# Revit family: Window-Exterior-Simpson-French-Sidelight
name_source: partatom
category: Windows
revit_build: Autodesk Revit Architecture 2012 (Build: 20110916_2132(x64)
units: mm (PartAtom-declared; Revit-internal decimal feet)

## types (1)
- Window-Exterior-Simpson-French-Sidelight
    Assembly Code = B2020100
    Bottom Panel Height = 15 3/8"
    Bottom Rail Height = 9 3/16"
    Default Sill Height = 0"
    Description = Exterior French - One Lite - Sidelight
    Glass = Glass - Simpson Doors - Clear
    Glass Options = http://simpsondoor.com
    Glass Thickness = 3/4"
    Height = 80 1/2"
    Horizontal Outside Lower = No
    Horizontal Outside Upper = No
    Innerbond Double Hip-Raised Panel = No
    Manufacturer = Simpson Door Company
    Middle Rail Height = 2 3/4"
    Model = 7701
    Muntin Width = 1 3/4"
    Number of Horizontal Muntins = 0
    Ovolo Construction = Yes
    Panel = Wood - Simpson Doors - Douglas Fir
    Panel Stile Width = 2 13/32"
    Product Documentation Link = http://www.simpsondoor.com
    Product Page URL = http://www.simpsondoor.com
    Rough Height = 0"
    Rough Width = 0"
    Thickness = 1 3/4"
    Top Panel = Glass - Simpson Doors - Clear
    Top Rail Height = 4 15/16"
    URL = http://www.simpsondoor.com
    UltraBlock Note = This Door Comes with The Option of UltraBlock Technology. It is Turn On as a Default
    UltraBlock Option = Yes
    Upper Muntin Offset = 6 1/8"
    Wall Closure = By host
    WaterBarrier Note = This Door Comes with The Option of WaterBarrier with UltraBlock Technology. It is Turn Off as a Default
    WaterBarrier with UltraBlock Technology = No
    Width = 14"
    Window Height = 48 1/4"
    Window Type = French-Full-Sidelight : Panel
    Wood Species = http://simpsondoor.com
    Wood Species Note = Available in Any Wood Species

## geometry (parser evidence)
native form markers: Sweep x16
no freeform markers — native parametric forms only
